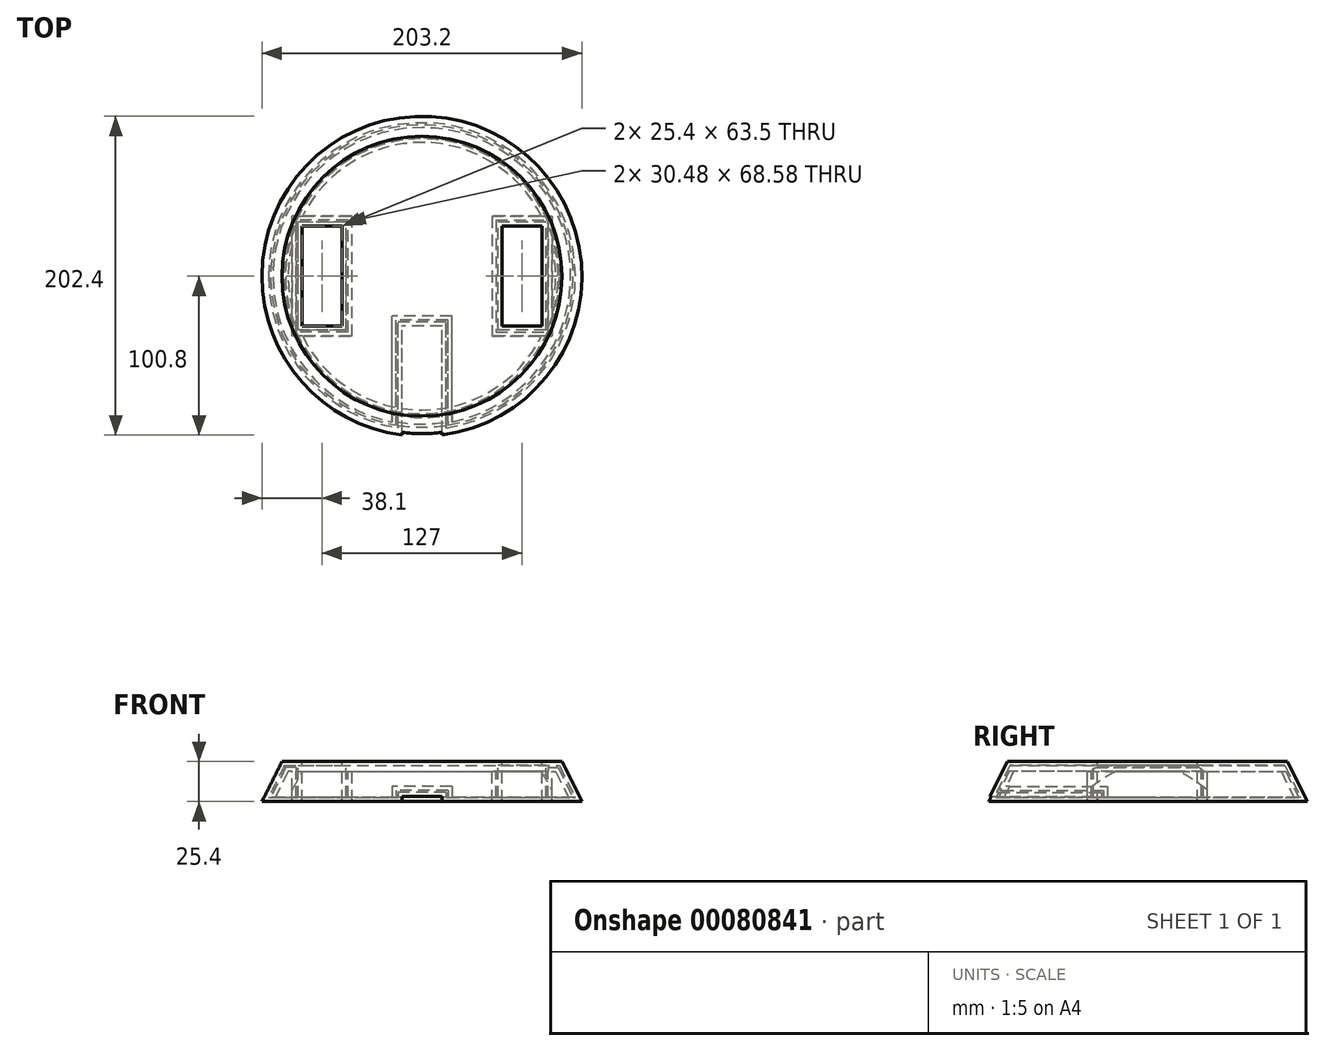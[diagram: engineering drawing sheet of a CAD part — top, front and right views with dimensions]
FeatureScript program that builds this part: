
annotation { "Feature Type Name" : "Feature", "Feature Type Description" : "" }
export const myFeature = defineFeature(function(context is Context, id is Id, definition is map)
    precondition{}
    {
        {
            var Q0;
            Q0=qCreatedBy(makeId("Front.planeOp"),FACE);
            var sketch = newSketch(context, id + "F0", { "sketchPlane" : qUnion([Q0])});
            skLineSegment(sketch, "E0", {"start": v(0, 25.4) * mm, "end": v(88.9, 25.4) * mm});
            skLineSegment(sketch, "E1", {"start": v(88.9, 25.4) * mm, "end": v(101.6, 0) * mm});
            skLineSegment(sketch, "E2", {"start": v(101.6, 0) * mm, "end": v(0, 0) * mm});
            skLineSegment(sketch, "E3", {"start": v(0, 0) * mm, "end": v(0, 25.4) * mm});
            skSolve(sketch);
        }
        {
            var Q0;
            Q0=makeQuery(id+"F0.imprint","IMPRINT",FACE,{"disambiguationData":[TD([[makeQuery(id+"F0.imprint","IMPRINT",EDGE,{"derivedFrom":sQuery(id+"F0.wireOp",EDGE,"E0")}),-1.0]])]});
            var Q1;
            Q1 = qConstructionFilter(qBodyType(qCreatedBy(id + "F0" ,EDGE), BodyType.WIRE), ConstructionObject.NO);
            var Q2;
            Q2=sQuery(id+"F0.wireOp",EDGE,"E3");
            revolve(context, id + "F1", {"entities" : qUnion([Q0]), "surfaceEntities" : qUnion([Q1]), "axis" : qUnion([Q2]), "revolveType" : RevolveType.FULL});
        }
        {
            var Q0;
            Q0=makeQuery(id+"F1.opRevolve","SWEPT_FACE",FACE,{"disambiguationData":[OSD([sQuery(id+"F0.wireOp",EDGE,"E0")])]});
            var sketch = newSketch(context, id + "F2", { "sketchPlane" : qUnion([Q0])});
            skLineSegment(sketch, "E4", {"start": v(0, -88.9) * mm, "end": v(0, 88.9) * mm, "construction": true});
            skLineSegment(sketch, "E5.bottom", {"start": v(-76.2, 31.75) * mm, "end": v(-50.8, 31.75) * mm});
            skLineSegment(sketch, "E5.top", {"start": v(-76.2, -31.75) * mm, "end": v(-50.8, -31.75) * mm});
            skLineSegment(sketch, "E5.left", {"start": v(-76.2, 31.75) * mm, "end": v(-76.2, -31.75) * mm});
            skLineSegment(sketch, "E5.right", {"start": v(-50.8, 31.75) * mm, "end": v(-50.8, -31.75) * mm});
            skLineSegment(sketch, "E6", {"start": v(-76.2, 0) * mm, "end": v(-50.8, 0) * mm, "construction": true});
            skLineSegment(sketch, "E7.MirrorCS", {"start": v(-50.8, -31.75) * mm, "end": v(-50.8, 31.75) * mm});
            skLineSegment(sketch, "E8.MirrorCS", {"start": v(-76.2, -31.75) * mm, "end": v(-76.2, 31.75) * mm});
            skLineSegment(sketch, "E9.MirrorCS", {"start": v(0, 88.9) * mm, "end": v(0, -88.9) * mm, "construction": true});
            skLineSegment(sketch, "E10.MirrorCS", {"start": v(76.2, 31.75) * mm, "end": v(50.8, 31.75) * mm});
            skLineSegment(sketch, "E11.MirrorCS", {"start": v(76.2, -31.75) * mm, "end": v(76.2, 31.75) * mm});
            skLineSegment(sketch, "E12.MirrorCS", {"start": v(76.2, -31.75) * mm, "end": v(50.8, -31.75) * mm});
            skLineSegment(sketch, "E13.MirrorCS", {"start": v(50.8, -31.75) * mm, "end": v(50.8, 31.75) * mm});
            skLineSegment(sketch, "E14.MirrorCS", {"start": v(76.2, 31.75) * mm, "end": v(76.2, -31.75) * mm});
            skLineSegment(sketch, "E15.MirrorCS", {"start": v(50.8, 31.75) * mm, "end": v(50.8, -31.75) * mm});
            skLineSegment(sketch, "E16.MirrorCS", {"start": v(76.2, 0) * mm, "end": v(50.8, 0) * mm, "construction": true});
            skSolve(sketch);
        }
        {
            var Q0;
            Q0 = qSketchRegion(id + "F2", true);
            extrude(context, id + "F3", {"entities" : qUnion([Q0]), "operationType" : NewBodyOperationType.REMOVE, "endBound" : BoundingType.UP_TO_NEXT, "oppositeDirection" : true, "depth" : 25.4 * mm});
        }
        {
            var Q0;
            Q0=makeQuery(id+"F3.boolean.opBoolean","COPY",FACE,{"derivedFrom":makeQuery(id+"F3.opExtrude","SWEPT_FACE",FACE,{"disambiguationData":[OSD([sQuery(id+"F2.wireOp",EDGE,"E12.MirrorCS")])]})});
            var sketch = newSketch(context, id + "F4", { "sketchPlane" : qUnion([Q0])});
            skLineSegment(sketch, "E17.bottom", {"start": v(-12.7, 3.18) * mm, "end": v(12.7, 3.18) * mm});
            skLineSegment(sketch, "E17.top", {"start": v(-12.7, 0) * mm, "end": v(12.7, 0) * mm});
            skLineSegment(sketch, "E17.left", {"start": v(-12.7, 3.18) * mm, "end": v(-12.7, 0) * mm});
            skLineSegment(sketch, "E17.right", {"start": v(12.7, 3.18) * mm, "end": v(12.7, 0) * mm});
            skSolve(sketch);
        }
        {
            var Q0;
            Q0 = qSketchRegion(id + "F4", true);
            extrude(context, id + "F5", {"entities" : qUnion([Q0]), "operationType" : NewBodyOperationType.REMOVE, "endBound" : BoundingType.THROUGH_ALL, "oppositeDirection" : true, "depth" : 25.4 * mm});
        }
        {
            var Q0;
            Q0=makeQuery(id+"F1.opRevolve","SWEPT_FACE",FACE,{"disambiguationData":[OSD([sQuery(id+"F0.wireOp",EDGE,"E2")])]});
            shell(context, id + "F6", {"entities" : qUnion([Q0]), "thickness" : 6.35 * mm});
        }
        {
            var Q0;
            Q0=makeQuery(id+"F6.opShell","OFFSET_FACE",FACE,{"disambiguationData":[OSD([sQuery(id+"F0.wireOp",EDGE,"E0")]),OD(2.0)]});
            shell(context, id + "F7", {"entities" : qUnion([Q0]), "thickness" : 2.54 * mm});
        }
    });
